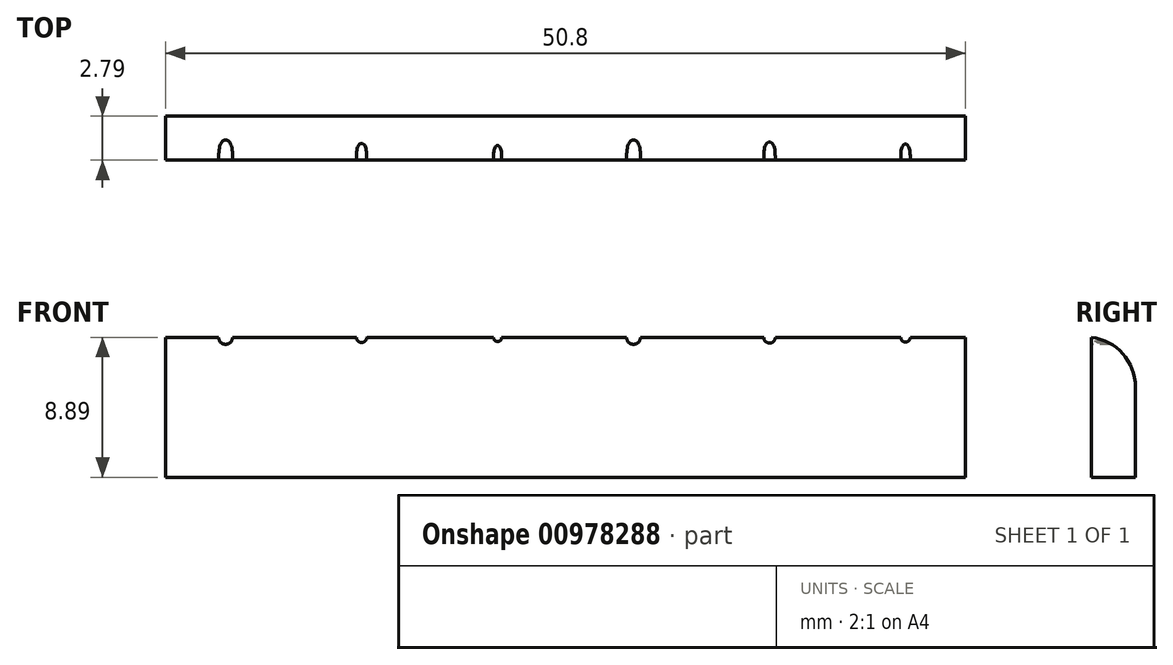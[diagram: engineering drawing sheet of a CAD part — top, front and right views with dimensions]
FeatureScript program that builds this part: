
annotation { "Feature Type Name" : "Feature", "Feature Type Description" : "" }
export const myFeature = defineFeature(function(context is Context, id is Id, definition is map)
    precondition{}
    {
        {
            var Q0;
            Q0=qCreatedBy(makeId("Top.planeOp"),FACE);
            var sketch = newSketch(context, id + "F0", { "sketchPlane" : qUnion([Q0])});
            skLineSegment(sketch, "E0.bottom", {"start": v(-25.4, 0) * mm, "end": v(25.4, 0) * mm});
            skLineSegment(sketch, "E0.top", {"start": v(-25.4, 2.8) * mm, "end": v(25.4, 2.8) * mm});
            skLineSegment(sketch, "E0.left", {"start": v(-25.4, 0) * mm, "end": v(-25.4, 2.8) * mm});
            skLineSegment(sketch, "E0.right", {"start": v(25.4, 0) * mm, "end": v(25.4, 2.8) * mm});
            skSolve(sketch);
        }
        {
            var Q0;
            Q0=makeQuery(id+"F0.imprint","IMPRINT",FACE,{"disambiguationData":[TD([[makeQuery(id+"F0.imprint","IMPRINT",EDGE,{"derivedFrom":sQuery(id+"F0.wireOp",EDGE,"E0.bottom")}),1.0]])]});
            extrude(context, id + "F1", {"entities" : qUnion([Q0]), "depth" : 8.9 * mm, "offsetDistance" : 25.4 * mm});
        }
        {
            var Q0;
            Q0=makeQuery(id+"F1.opExtrude","CAP_EDGE",EDGE,{"disambiguationData":[OSD([sQuery(id+"F0.wireOp",EDGE,"E0.top")])],"isStart":false});
            fillet(context, id + "F2", {"entities" : qUnion([Q0]), "tangentPropagation" : true, "radius" : 3.17 * mm, "defaultsChanged" : true, "vertexSettings" : [], "allowEdgeOverflow" : false});
        }
        {
            var Q0;
            Q0=makeQuery(id+"F1.opExtrude","SWEPT_FACE",FACE,{"disambiguationData":[OSD([sQuery(id+"F0.wireOp",EDGE,"E0.bottom")])]});
            var sketch = newSketch(context, id + "F3", { "sketchPlane" : qUnion([Q0])});
            skCircle(sketch, "E1", {"center": v(-21.59, 8.9) * mm, "radius": 0.44 * mm});
            skCircle(sketch, "E2", {"center": v(-12.95, 8.9) * mm, "radius": 0.33 * mm});
            skCircle(sketch, "E3", {"center": v(12.95, 8.9) * mm, "radius": 0.37 * mm});
            skCircle(sketch, "E4", {"center": v(21.59, 8.9) * mm, "radius": 0.3 * mm});
            skCircle(sketch, "E5", {"center": v(-4.32, 8.9) * mm, "radius": 0.27 * mm});
            skCircle(sketch, "E6", {"center": v(4.32, 8.9) * mm, "radius": 0.44 * mm});
            skSolve(sketch);
        }
        {
            var Q0;
            {var subQ0=sQuery(id+"F3.wireOp",EDGE,"E1");var subQ1=makeQuery(id+"F2.opFillet","BLEND_EDGE",EDGE,{"blendedFrom":[makeQuery(id+"F1.opExtrude","CAP_EDGE",EDGE,{"disambiguationData":[OSD([sQuery(id+"F0.wireOp",EDGE,"E0.top")])],"isStart":false}),makeQuery(id+"F1.opExtrude","SWEPT_FACE",FACE,{"disambiguationData":[OSD([sQuery(id+"F0.wireOp",EDGE,"E0.bottom")])]})],"blendedInto":[makeQuery(id+"F1.opExtrude","SWEPT_FACE",FACE,{"disambiguationData":[OSD([sQuery(id+"F0.wireOp",EDGE,"E0.bottom")])]})]});var subQ2=makeQuery(id+"F3.imprint","INTERSECT",VERTEX,{"disambiguationData":[OD(0.0)],"derivedFrom":[subQ1,subQ0]});Q0=makeQuery(id+"F3.imprint","IMPRINT",FACE,{"disambiguationData":[TD([[makeQuery(id+"F3.imprint","IMPRINT",EDGE,{"disambiguationData":[TD([[subQ2,-1.0]])],"derivedFrom":subQ0}),1.0]])]});}
            var Q1;
            {var subQ0=sQuery(id+"F3.wireOp",EDGE,"E2");var subQ1=makeQuery(id+"F2.opFillet","BLEND_EDGE",EDGE,{"blendedFrom":[makeQuery(id+"F1.opExtrude","CAP_EDGE",EDGE,{"disambiguationData":[OSD([sQuery(id+"F0.wireOp",EDGE,"E0.top")])],"isStart":false}),makeQuery(id+"F1.opExtrude","SWEPT_FACE",FACE,{"disambiguationData":[OSD([sQuery(id+"F0.wireOp",EDGE,"E0.bottom")])]})],"blendedInto":[makeQuery(id+"F1.opExtrude","SWEPT_FACE",FACE,{"disambiguationData":[OSD([sQuery(id+"F0.wireOp",EDGE,"E0.bottom")])]})]});var subQ2=makeQuery(id+"F3.imprint","INTERSECT",VERTEX,{"disambiguationData":[OD(0.0)],"derivedFrom":[subQ1,subQ0]});Q1=makeQuery(id+"F3.imprint","IMPRINT",FACE,{"disambiguationData":[TD([[makeQuery(id+"F3.imprint","IMPRINT",EDGE,{"disambiguationData":[TD([[subQ2,-1.0]])],"derivedFrom":subQ0}),1.0]])]});}
            var Q2;
            {var subQ0=sQuery(id+"F3.wireOp",EDGE,"E3");var subQ1=makeQuery(id+"F2.opFillet","BLEND_EDGE",EDGE,{"blendedFrom":[makeQuery(id+"F1.opExtrude","CAP_EDGE",EDGE,{"disambiguationData":[OSD([sQuery(id+"F0.wireOp",EDGE,"E0.top")])],"isStart":false}),makeQuery(id+"F1.opExtrude","SWEPT_FACE",FACE,{"disambiguationData":[OSD([sQuery(id+"F0.wireOp",EDGE,"E0.bottom")])]})],"blendedInto":[makeQuery(id+"F1.opExtrude","SWEPT_FACE",FACE,{"disambiguationData":[OSD([sQuery(id+"F0.wireOp",EDGE,"E0.bottom")])]})]});var subQ2=makeQuery(id+"F3.imprint","INTERSECT",VERTEX,{"disambiguationData":[OD(0.0)],"derivedFrom":[subQ1,subQ0]});Q2=makeQuery(id+"F3.imprint","IMPRINT",FACE,{"disambiguationData":[TD([[makeQuery(id+"F3.imprint","IMPRINT",EDGE,{"disambiguationData":[TD([[subQ2,1.0]])],"derivedFrom":subQ0}),1.0]])]});}
            var Q3;
            {var subQ0=sQuery(id+"F3.wireOp",EDGE,"E4");var subQ1=makeQuery(id+"F2.opFillet","BLEND_EDGE",EDGE,{"blendedFrom":[makeQuery(id+"F1.opExtrude","CAP_EDGE",EDGE,{"disambiguationData":[OSD([sQuery(id+"F0.wireOp",EDGE,"E0.top")])],"isStart":false}),makeQuery(id+"F1.opExtrude","SWEPT_FACE",FACE,{"disambiguationData":[OSD([sQuery(id+"F0.wireOp",EDGE,"E0.bottom")])]})],"blendedInto":[makeQuery(id+"F1.opExtrude","SWEPT_FACE",FACE,{"disambiguationData":[OSD([sQuery(id+"F0.wireOp",EDGE,"E0.bottom")])]})]});var subQ2=makeQuery(id+"F3.imprint","INTERSECT",VERTEX,{"disambiguationData":[OD(0.0)],"derivedFrom":[subQ1,subQ0]});Q3=makeQuery(id+"F3.imprint","IMPRINT",FACE,{"disambiguationData":[TD([[makeQuery(id+"F3.imprint","IMPRINT",EDGE,{"disambiguationData":[TD([[subQ2,1.0]])],"derivedFrom":subQ0}),1.0]])]});}
            var Q4;
            {var subQ0=sQuery(id+"F3.wireOp",EDGE,"E5");var subQ1=makeQuery(id+"F2.opFillet","BLEND_EDGE",EDGE,{"blendedFrom":[makeQuery(id+"F1.opExtrude","CAP_EDGE",EDGE,{"disambiguationData":[OSD([sQuery(id+"F0.wireOp",EDGE,"E0.top")])],"isStart":false}),makeQuery(id+"F1.opExtrude","SWEPT_FACE",FACE,{"disambiguationData":[OSD([sQuery(id+"F0.wireOp",EDGE,"E0.bottom")])]})],"blendedInto":[makeQuery(id+"F1.opExtrude","SWEPT_FACE",FACE,{"disambiguationData":[OSD([sQuery(id+"F0.wireOp",EDGE,"E0.bottom")])]})]});var subQ2=makeQuery(id+"F3.imprint","INTERSECT",VERTEX,{"disambiguationData":[OD(0.0)],"derivedFrom":[subQ1,subQ0]});Q4=makeQuery(id+"F3.imprint","IMPRINT",FACE,{"disambiguationData":[TD([[makeQuery(id+"F3.imprint","IMPRINT",EDGE,{"disambiguationData":[TD([[subQ2,-1.0]])],"derivedFrom":subQ0}),1.0]])]});}
            var Q5;
            {var subQ0=sQuery(id+"F3.wireOp",EDGE,"E6");var subQ1=makeQuery(id+"F2.opFillet","BLEND_EDGE",EDGE,{"blendedFrom":[makeQuery(id+"F1.opExtrude","CAP_EDGE",EDGE,{"disambiguationData":[OSD([sQuery(id+"F0.wireOp",EDGE,"E0.top")])],"isStart":false}),makeQuery(id+"F1.opExtrude","SWEPT_FACE",FACE,{"disambiguationData":[OSD([sQuery(id+"F0.wireOp",EDGE,"E0.bottom")])]})],"blendedInto":[makeQuery(id+"F1.opExtrude","SWEPT_FACE",FACE,{"disambiguationData":[OSD([sQuery(id+"F0.wireOp",EDGE,"E0.bottom")])]})]});var subQ2=makeQuery(id+"F3.imprint","INTERSECT",VERTEX,{"disambiguationData":[OD(0.0)],"derivedFrom":[subQ1,subQ0]});Q5=makeQuery(id+"F3.imprint","IMPRINT",FACE,{"disambiguationData":[TD([[makeQuery(id+"F3.imprint","IMPRINT",EDGE,{"disambiguationData":[TD([[subQ2,1.0]])],"derivedFrom":subQ0}),1.0]])]});}
            extrude(context, id + "F4", {"entities" : qUnion([Q0, Q1, Q2, Q3, Q4, Q5]), "operationType" : NewBodyOperationType.REMOVE, "oppositeDirection" : true, "depth" : 25.4 * mm, "offsetDistance" : 25.4 * mm});
        }
    });
